# Revit family: Hager-FW-IP30-With_Door-Closed-syst-AT-de
name_source: partatom
category: Electrical Equipment
units: mm (PartAtom-declared; Revit-internal decimal feet)

## family parameters
Cut with Voids When Loaded = No
Host = Face
Panel Configuration = Two Columns, Circuits Across
Part Type = Panelboard
Room Calculation Point = No
Round Connector Dimension = Use Diameter
Shared = No

## types (3) — shared parameters
EF000003 - Montageart = EV000128 - Hohlwand
EF000007 - Farbe = EV000202 - weiß
EF000008 - Breite = 603 mm
EF000049 - Tiefe = 125 mm  [stored 0.410105 ft]
EF000116 - RAL-Nummer = 9010
EF000118 - Mit Montageplatte = Yes
EF000218 - Einbautiefe = 112 mm  [stored 0.367454 ft]
EF000339 - Art der Abdeckung = EV004216 - Tür
EF000846 - Einbaubreite = 560 mm  [stored 1.83727 ft]
EF001062 - EMV-Ausführung = No
EF001088 - Anbaumöglichkeit = Yes
EF001131 - Innentiefe = 110 mm
EF001134 - DIN-Schiene = Yes
EF001596 - Werkstoff des Gehäuses = EV000179 - Stahl
EF002950 - Breite in Teilungseinheiten = 12
EF005474 - Schutzart (IP) = EV006410 - IP30
EF006244 - Transparenter Deckel/Tür = No
EF006306 - Mit Schloss = No
EF015776 - Erdungsklemmenblock = Yes
EF015777 - Neutralleiterklemmenblock = Yes
EF015941 - Signaldurchlassende Tür = Yes
HG000001 - Anzahl der Spalten = 1
HG000002 - Mit tür = Yes
HG000003 - Bereich = FW
HG000005 - Dicke = 3 mm  [stored 0.00984252 ft]
HG000006 - Unterputz = Yes
HG000007 - Anzahl der leeren Spalten = 1
HG000009 - Doppelflügeligen Tür = No
HG000010 - Asymmetrische Türen = No
HG000011 - Leere Reihen von unten = No
HG000017 - Distanz zwischen den Polen = 18 mm  [stored 0.0590551 ft]
Manufacturer = Hager
Type Comments = FW
zero-valued in all types: Default Elevation

## per-type parameters (varying)
| type | EF000040 - Höhe | EF000266 - Anzahl der Reihen | EF000332 - Einbauhöhe | EF004462 - Art der Schließung | EF009212 - Ausführung Deckel | HG000004 - Herstellerreferenz | HG000008 - Anzahl der leeren Reihen | Model |
| Unterputz IP30 B603 H1003 T125 12 Teilungseinheiten - FWU62K3 | 1003 mm | 6 | 952 mm |  | EV000116 - geschlossen | FWU62K3 | 6 | FWU62K3 |
| Unterputz IP30 B603 H703 T125 12 Teilungseinheiten - FWU42K3 | 703 mm | 4 | 652 mm | EV000154 - sonstige | EV009916 - mit Ausschnitt | FWU42K3 | 4 | FWU42K3 |
| Unterputz IP30 B603 H853 T125 12 Teilungseinheiten - FWU52K3 | 853 mm  [stored 2.79856 ft] | 5 | 802 mm  [stored 2.63123 ft] | EV000154 - sonstige | EV009916 - mit Ausschnitt | FWU52K3 | 5 | FWU52K3 |

note: [stored X ft] marks values corroborated as IEEE doubles in the binary element streams (Revit-internal decimal feet)

## geometry (parser evidence)
native form markers: Sweep x17
no freeform markers — native parametric forms only
